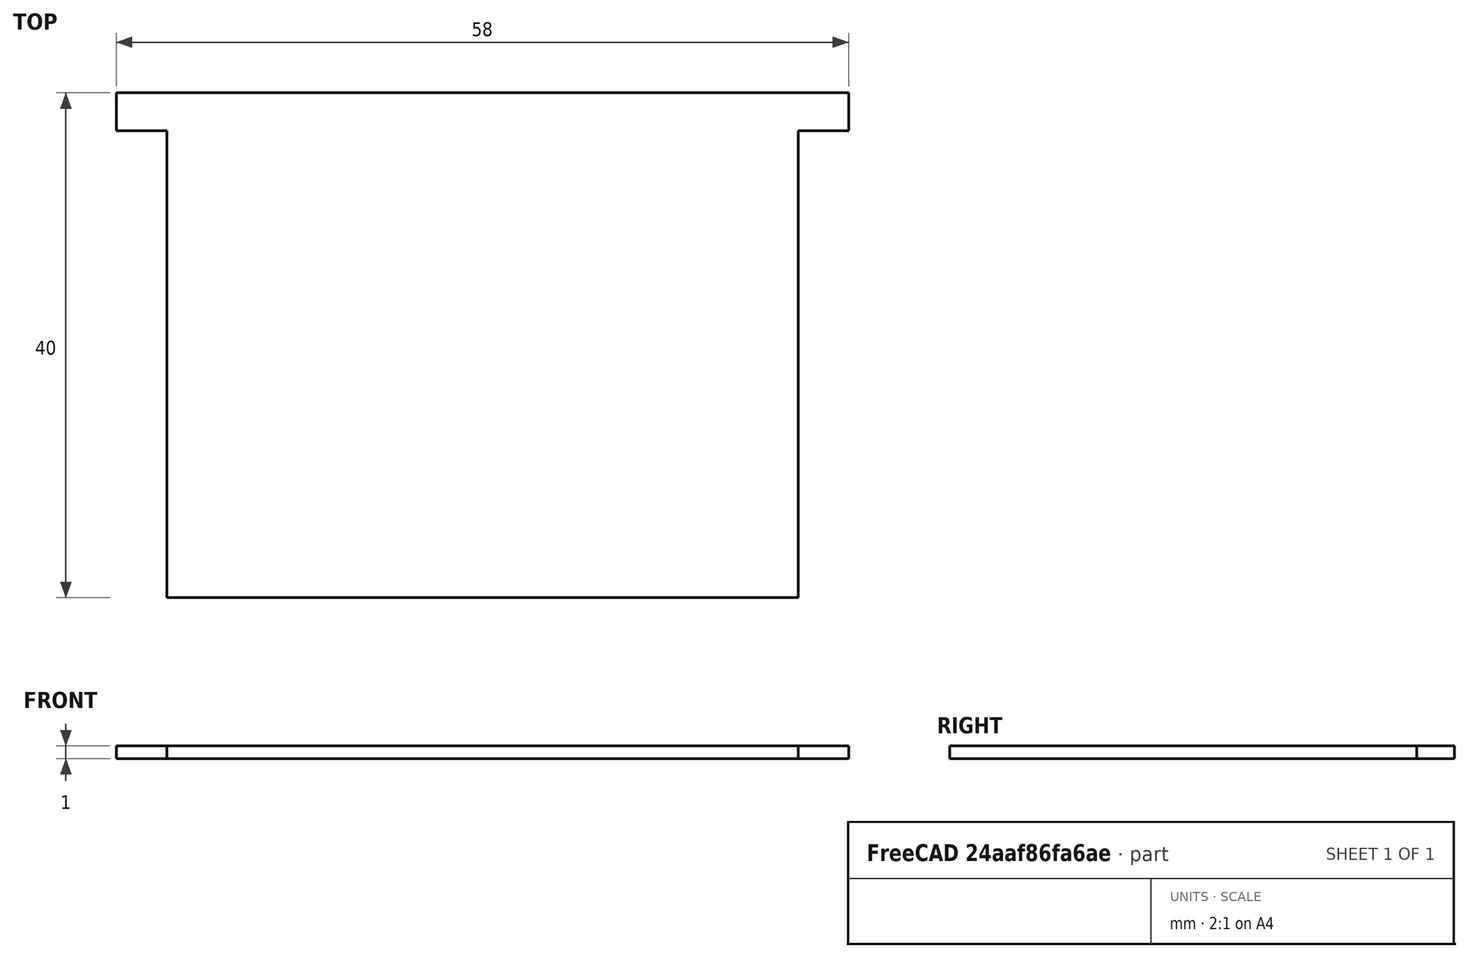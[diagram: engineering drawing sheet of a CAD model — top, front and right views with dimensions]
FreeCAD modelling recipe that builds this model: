
FCSTD DOCUMENT  (FreeCAD 1.0R39109 (Git))
Label: flatFlap
License: All rights reserved
LicenseURL: https://en.wikipedia.org/wiki/All_rights_reserved
objects: Sketcher::SketchObject×1, PartDesign::Pad×1, PartDesign::Body×1
note: 6 computed .brp shape members not serialized (recipe doc carries the construction recipe); baked Part::Feature solids carry a one-line shape summary decoded from their .brp

FEATURE [Sketcher::SketchObject] Sketch
  ArcFitTolerance = 1e-06
  AttachmentSupport = -> [XY_Plane]
  FullyConstrained = true
  MakeInternals = false
  MapMode = 5
  sketch-geometry (12):
    g0: GeomPoint [constr] X=0 Y=0 Z=0
    g1: LineSegment StartX=-25 StartY=-20 StartZ=0 EndX=25 EndY=-20 EndZ=0
    g2: LineSegment StartX=25 StartY=-20 StartZ=0 EndX=25 EndY=17 EndZ=0
    g3: LineSegment StartX=25 StartY=20 StartZ=0 EndX=-25 EndY=20 EndZ=0
    g4: LineSegment StartX=-25 StartY=17 StartZ=0 EndX=-25 EndY=-20 EndZ=0
    g5: GeomPoint [constr] X=0 Y=0 Z=0
    g6: LineSegment StartX=25 StartY=17 StartZ=0 EndX=29 EndY=17 EndZ=0
    g7: LineSegment StartX=29 StartY=17 StartZ=0 EndX=29 EndY=20 EndZ=0
    g8: LineSegment StartX=29 StartY=20 StartZ=0 EndX=25 EndY=20 EndZ=0
    g9: LineSegment StartX=-25 StartY=20 StartZ=0 EndX=-29 EndY=20 EndZ=0
    g10: LineSegment StartX=-29 StartY=20 StartZ=0 EndX=-29 EndY=17 EndZ=0
    g11: LineSegment StartX=-29 StartY=17 StartZ=0 EndX=-25 EndY=17 EndZ=0
  constraints (31):
    c: Coincident(g0,g-1)
    c: Coincident(g1,g2)
    c: Coincident(g4,g1)
    c: Horizontal(g1)
    c: Horizontal(g3)
    c: Vertical(g2)
    c: Vertical(g4)
    c: Symmetric(g3,g1,g5)
    c: Coincident(g5,g0)
    c: Coincident(g6,g7)
    c: Coincident(g7,g8)
    c: Vertical(g7)
    c: Horizontal(g6)
    c: Horizontal(g8)
    c: Coincident(g9,g10)
    c: Coincident(g10,g11)
    c: Horizontal(g9)
    c: Horizontal(g11)
    c: Vertical(g10)
    c: Coincident(g9,g3)
    c: Coincident(g4,g11)
    c: Coincident(g3,g8)
    c: Coincident(g2,g6)
    c: Distance(g10,g10) = 3
    c: DistanceX(g9,g9) = 4
    c: Distance(g11,g11) = 4
    c: DistanceX(g8,g8) = 4
    c: DistanceY(g7,g7) = 3
    c: Distance(g6,g6) = 4
    c: Distance(g1,g3) = 40
    c: DistanceX(g1,g1) = 50
FEATURE [PartDesign::Pad] Pad
  Direction = (0,0,1)
  Length = 1
  Length2 = 10
  Profile = -> Sketch
  ReferenceAxis = -> Sketch [N_Axis]
  Refine = true
  Suppressed = false
  Type = 0
FEATURE [PartDesign::Body] Body
  AllowCompound = false
  Group = -> [Sketch,Pad]
  Origin = -> Origin
  Tip = -> Pad
